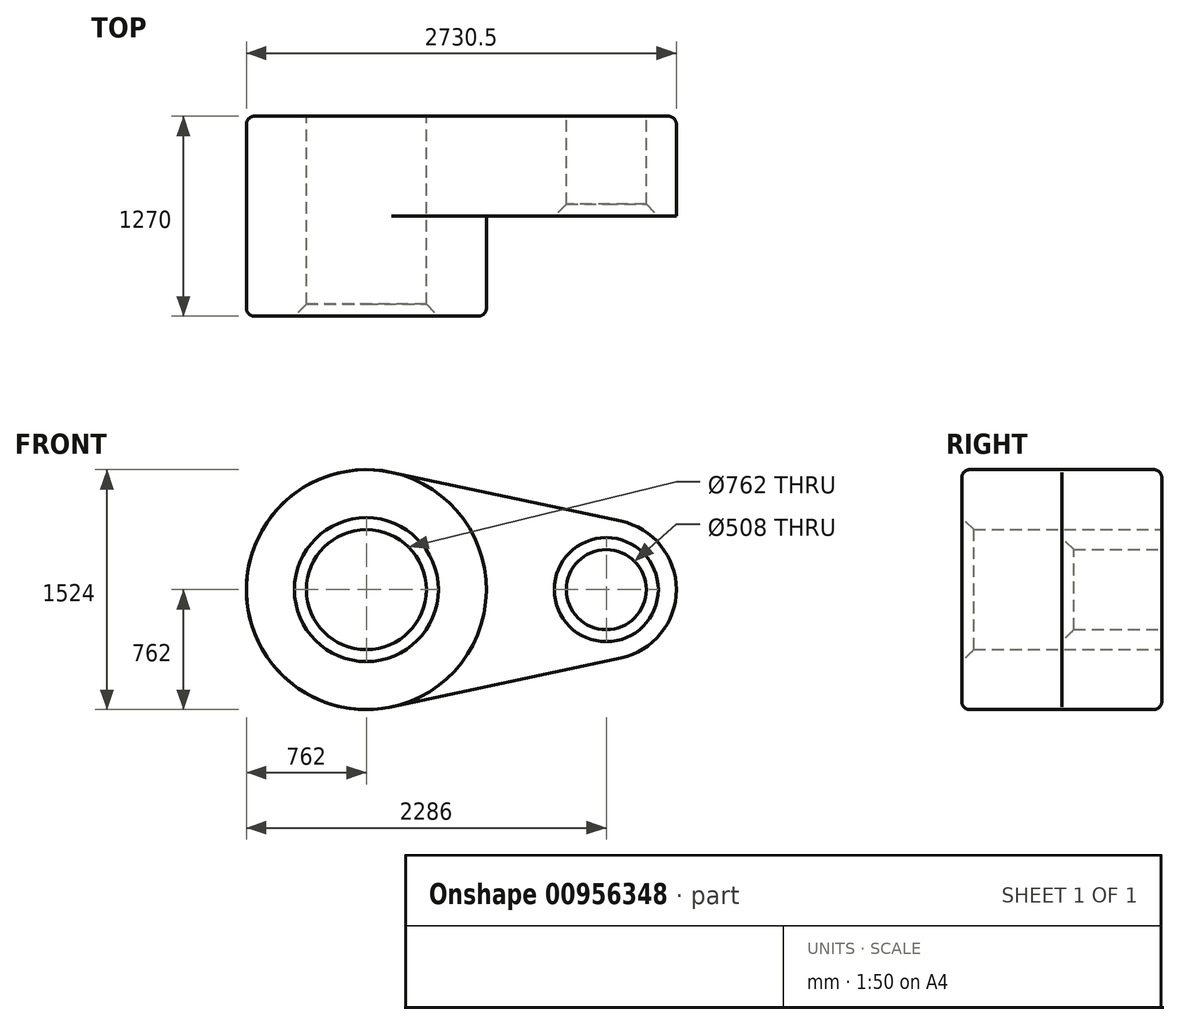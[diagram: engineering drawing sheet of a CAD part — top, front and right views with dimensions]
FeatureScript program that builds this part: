
annotation { "Feature Type Name" : "Feature", "Feature Type Description" : "" }
export const myFeature = defineFeature(function(context is Context, id is Id, definition is map)
    precondition{}
    {
        {
            var Q0;
            Q0=qCreatedBy(makeId("Front.planeOp"),FACE);
            var sketch = newSketch(context, id + "F0", { "sketchPlane" : qUnion([Q0])});
            skCircle(sketch, "E0", {"center": v(0, 0) * mm, "radius": 762 * mm});
            skCircle(sketch, "E1", {"center": v(1524, 0) * mm, "radius": 444.5 * mm});
            skLineSegment(sketch, "E2", {"start": v(158.75, 745.28) * mm, "end": v(1616.6, 434.75) * mm});
            skLineSegment(sketch, "E3", {"start": v(158.75, -745.28) * mm, "end": v(1616.6, -434.75) * mm});
            skCircle(sketch, "E4", {"center": v(0, 0) * mm, "radius": 381 * mm});
            skCircle(sketch, "E5", {"center": v(1524, 0) * mm, "radius": 254 * mm});
            skSolve(sketch);
        }
        {
            var Q0;
            Q0=qSketchRegion(id+"F0",true);
            extrude(context, id + "F1", {"entities" : qUnion([Q0]), "depth" : 635 * mm, "offsetDistance" : 25.4 * mm});
        }
        {
            var Q0;
            Q0=makeQuery(id+"F0.imprint","IMPRINT",FACE,{"disambiguationData":[TD([[makeQuery(id+"F0.imprint","IMPRINT",EDGE,{"derivedFrom":sQuery(id+"F0.wireOp",EDGE,"E4")}),-1.0]])]});
            extrude(context, id + "F2", {"entities" : qUnion([Q0]), "operationType" : NewBodyOperationType.ADD, "depth" : 1270 * mm, "offsetDistance" : 25.4 * mm});
        }
        {
            var Q0;
            Q0=makeQuery(id+"F2.opExtrude","CAP_EDGE",EDGE,{"disambiguationData":[OSD([sQuery(id+"F0.wireOp",EDGE,"E0")])],"isStart":false});
            var Q1;
            Q1=makeQuery(id+"F1.opExtrude","CAP_EDGE",EDGE,{"disambiguationData":[OSD([sQuery(id+"F0.wireOp",EDGE,"E3")])],"isStart":true});
            fillet(context, id + "F3", {"entities" : qUnion([Q0, Q1]), "radius" : 50.8 * mm, "tangentPropagation" : true, "allowEdgeOverflow" : false});
        }
        {
            var Q0;
            Q0=makeQuery(id+"F2.opExtrude","CAP_EDGE",EDGE,{"disambiguationData":[OSD([sQuery(id+"F0.wireOp",EDGE,"E4")])],"isStart":false});
            var Q1;
            Q1=makeQuery(id+"F1.opExtrude","CAP_EDGE",EDGE,{"disambiguationData":[OSD([sQuery(id+"F0.wireOp",EDGE,"E5")])],"isStart":false});
            chamfer(context, id + "F4", {"entities" : qUnion([Q0, Q1]), "width" : 76.2 * mm, "tangentPropagation" : true});
        }
    });
